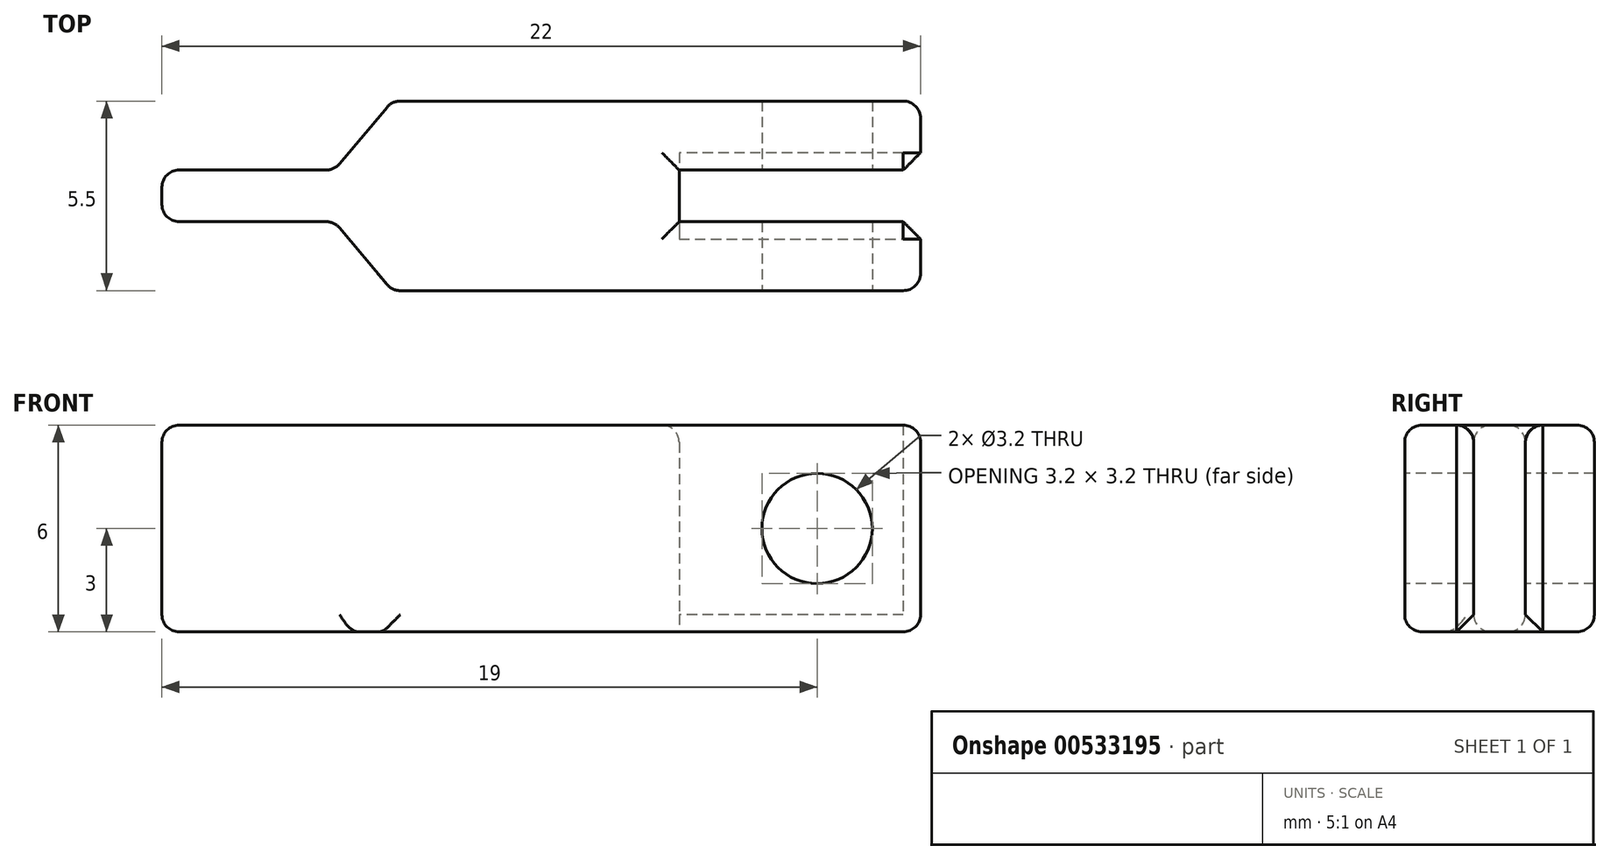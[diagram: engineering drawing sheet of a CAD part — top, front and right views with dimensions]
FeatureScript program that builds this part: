
annotation { "Feature Type Name" : "Feature", "Feature Type Description" : "" }
export const myFeature = defineFeature(function(context is Context, id is Id, definition is map)
    precondition{}
    {
        {
            var Q0;
            Q0=qCreatedBy(makeId("Top.planeOp"),FACE);
            var sketch = newSketch(context, id + "F0", { "sketchPlane" : qUnion([Q0])});
            skLineSegment(sketch, "E0", {"start": v(0, 0) * mm, "end": v(-15.32, 0) * mm});
            skLineSegment(sketch, "E1", {"start": v(-15.32, 0) * mm, "end": v(-17, 2) * mm});
            skLineSegment(sketch, "E2", {"start": v(-17, 2) * mm, "end": v(-22, 2) * mm});
            skLineSegment(sketch, "E3", {"start": v(-22, 2) * mm, "end": v(-22, 3.5) * mm});
            skLineSegment(sketch, "E4", {"start": v(-22, 3.5) * mm, "end": v(-17, 3.5) * mm});
            skLineSegment(sketch, "E5", {"start": v(-17, 3.5) * mm, "end": v(-15.32, 5.5) * mm});
            skLineSegment(sketch, "E6", {"start": v(-15.32, 5.5) * mm, "end": v(0, 5.5) * mm});
            skLineSegment(sketch, "E7", {"start": v(0, 5.5) * mm, "end": v(0, 3.5) * mm});
            skLineSegment(sketch, "E8", {"start": v(0, 3.5) * mm, "end": v(-7, 3.5) * mm});
            skLineSegment(sketch, "E9", {"start": v(-7, 3.5) * mm, "end": v(-7, 2) * mm});
            skLineSegment(sketch, "E10", {"start": v(-7, 2) * mm, "end": v(0, 2) * mm});
            skLineSegment(sketch, "E11", {"start": v(0, 2) * mm, "end": v(0, 0) * mm});
            skSolve(sketch);
        }
        {
            var Q0;
            Q0=makeQuery(id+"F0.imprint","IMPRINT",FACE,{"disambiguationData":[TD([[makeQuery(id+"F0.imprint","IMPRINT",EDGE,{"derivedFrom":sQuery(id+"F0.wireOp",EDGE,"E0")}),-1.0]])]});
            extrude(context, id + "F1", {"entities" : qUnion([Q0]), "depth" : 6 * mm, "offsetDistance" : 25 * mm});
        }
        {
            var Q0;
            Q0=makeQuery(id+"F1.opExtrude","SWEPT_FACE",FACE,{"disambiguationData":[OSD([sQuery(id+"F0.wireOp",EDGE,"E0")])]});
            var sketch = newSketch(context, id + "F2", { "sketchPlane" : qUnion([Q0])});
            skLineSegment(sketch, "E12", {"start": v(0, 3) * mm, "end": v(-15.32, 3) * mm, "construction": true});
            skCircle(sketch, "E13", {"center": v(-3, 3) * mm, "radius": 1.6 * mm});
            skSolve(sketch);
        }
        {
            var Q0;
            Q0=sQuery(id+"F2.wireOp",VERTEX,"E13.center");
            var Q1;
            Q1=makeQuery(id+"F1.opExtrude","SWEPT_BODY",BODY,{"disambiguationData":[OSD([sQuery(id+"F0.wireOp",EDGE,"E0"),sQuery(id+"F0.wireOp",EDGE,"E1"),sQuery(id+"F0.wireOp",EDGE,"E2"),sQuery(id+"F0.wireOp",EDGE,"E3"),sQuery(id+"F0.wireOp",EDGE,"E4"),sQuery(id+"F0.wireOp",EDGE,"E5"),sQuery(id+"F0.wireOp",EDGE,"E6"),sQuery(id+"F0.wireOp",EDGE,"E7"),sQuery(id+"F0.wireOp",EDGE,"E8"),sQuery(id+"F0.wireOp",EDGE,"E9"),sQuery(id+"F0.wireOp",EDGE,"E10"),sQuery(id+"F0.wireOp",EDGE,"E11")])]});
            hole(context, id + "F3", {"style" : HoleStyle.SIMPLE, "endStyle" : HoleEndStyle.THROUGH, "holeDiameter" : 3.2 * mm, "isTappedThrough" : true, "tappedDepth" : 12 * mm, "tapClearance" : 3, "locations" : qUnion([Q0]), "scope" : qUnion([Q1])});
        }
        {
            var Q0;
            Q0=makeQuery(id+"F1.opExtrude","SWEPT_EDGE",EDGE,{"disambiguationData":[OSD([sQuery(id+"F0.wireOp",EDGE,"E1"),sQuery(id+"F0.wireOp",EDGE,"E2")])]});
            var Q1;
            Q1=makeQuery(id+"F1.opExtrude","SWEPT_EDGE",EDGE,{"disambiguationData":[OSD([sQuery(id+"F0.wireOp",EDGE,"E0"),sQuery(id+"F0.wireOp",EDGE,"E1")])]});
            var Q2;
            Q2=makeQuery(id+"F1.opExtrude","SWEPT_EDGE",EDGE,{"disambiguationData":[OSD([sQuery(id+"F0.wireOp",EDGE,"E0"),sQuery(id+"F0.wireOp",EDGE,"E11")])]});
            var Q3;
            Q3=makeQuery(id+"F1.opExtrude","SWEPT_EDGE",EDGE,{"disambiguationData":[OSD([sQuery(id+"F0.wireOp",EDGE,"E6"),sQuery(id+"F0.wireOp",EDGE,"E7")])]});
            var Q4;
            Q4=makeQuery(id+"F1.opExtrude","SWEPT_EDGE",EDGE,{"disambiguationData":[OSD([sQuery(id+"F0.wireOp",EDGE,"E5"),sQuery(id+"F0.wireOp",EDGE,"E6")])]});
            var Q5;
            Q5=makeQuery(id+"F1.opExtrude","SWEPT_EDGE",EDGE,{"disambiguationData":[OSD([sQuery(id+"F0.wireOp",EDGE,"E4"),sQuery(id+"F0.wireOp",EDGE,"E5")])]});
            var Q6;
            Q6=makeQuery(id+"F1.opExtrude","CAP_EDGE",EDGE,{"disambiguationData":[OSD([sQuery(id+"F0.wireOp",EDGE,"E6")])],"isStart":true});
            var Q7;
            Q7=makeQuery(id+"F1.opExtrude","CAP_EDGE",EDGE,{"disambiguationData":[OSD([sQuery(id+"F0.wireOp",EDGE,"E5")])],"isStart":true});
            var Q8;
            Q8=makeQuery(id+"F1.opExtrude","CAP_EDGE",EDGE,{"disambiguationData":[OSD([sQuery(id+"F0.wireOp",EDGE,"E4")])],"isStart":true});
            var Q9;
            Q9=makeQuery(id+"F1.opExtrude","CAP_EDGE",EDGE,{"disambiguationData":[OSD([sQuery(id+"F0.wireOp",EDGE,"E2")])],"isStart":true});
            var Q10;
            Q10=makeQuery(id+"F1.opExtrude","CAP_EDGE",EDGE,{"disambiguationData":[OSD([sQuery(id+"F0.wireOp",EDGE,"E0")])],"isStart":true});
            var Q11;
            Q11=makeQuery(id+"F1.opExtrude","CAP_EDGE",EDGE,{"disambiguationData":[OSD([sQuery(id+"F0.wireOp",EDGE,"E11")])],"isStart":true});
            var Q12;
            Q12=makeQuery(id+"F1.opExtrude","CAP_EDGE",EDGE,{"disambiguationData":[OSD([sQuery(id+"F0.wireOp",EDGE,"E7")])],"isStart":true});
            var Q13;
            Q13=makeQuery(id+"F1.opExtrude","CAP_FACE",FACE,{"disambiguationData":[OSD([sQuery(id+"F0.wireOp",EDGE,"E0"),sQuery(id+"F0.wireOp",EDGE,"E1"),sQuery(id+"F0.wireOp",EDGE,"E2"),sQuery(id+"F0.wireOp",EDGE,"E3"),sQuery(id+"F0.wireOp",EDGE,"E4"),sQuery(id+"F0.wireOp",EDGE,"E5"),sQuery(id+"F0.wireOp",EDGE,"E6"),sQuery(id+"F0.wireOp",EDGE,"E7"),sQuery(id+"F0.wireOp",EDGE,"E8"),sQuery(id+"F0.wireOp",EDGE,"E9"),sQuery(id+"F0.wireOp",EDGE,"E10"),sQuery(id+"F0.wireOp",EDGE,"E11")])],"isStart":false});
            var Q14;
            Q14=makeQuery(id+"F1.opExtrude","CAP_EDGE",EDGE,{"disambiguationData":[OSD([sQuery(id+"F0.wireOp",EDGE,"E3")])],"isStart":false});
            var Q15;
            Q15=makeQuery(id+"F1.opExtrude","CAP_EDGE",EDGE,{"disambiguationData":[OSD([sQuery(id+"F0.wireOp",EDGE,"E3")])],"isStart":true});
            var Q16;
            Q16=makeQuery(id+"F1.opExtrude","SWEPT_EDGE",EDGE,{"disambiguationData":[OSD([sQuery(id+"F0.wireOp",EDGE,"E2"),sQuery(id+"F0.wireOp",EDGE,"E3")])]});
            var Q17;
            Q17=makeQuery(id+"F1.opExtrude","SWEPT_EDGE",EDGE,{"disambiguationData":[OSD([sQuery(id+"F0.wireOp",EDGE,"E3"),sQuery(id+"F0.wireOp",EDGE,"E4")])]});
            fillet(context, id + "F4", {"entities" : qUnion([Q0, Q1, Q2, Q3, Q4, Q5, Q6, Q7, Q8, Q9, Q10, Q11, Q12, Q13, Q14, Q15, Q16, Q17]), "radius" : 0.5 * mm, "tangentPropagation" : true, "allowEdgeOverflow" : false});
        }
        {
            var Q0;
            Q0=makeQuery(id+"F1.opExtrude","SWEPT_EDGE",EDGE,{"disambiguationData":[OSD([sQuery(id+"F0.wireOp",EDGE,"E10"),sQuery(id+"F0.wireOp",EDGE,"E11")])]});
            var Q1;
            Q1=makeQuery(id+"F1.opExtrude","SWEPT_EDGE",EDGE,{"disambiguationData":[OSD([sQuery(id+"F0.wireOp",EDGE,"E7"),sQuery(id+"F0.wireOp",EDGE,"E8")])]});
            chamfer(context, id + "F5", {"entities" : qUnion([Q0, Q1]), "width" : 0.5 * mm, "tangentPropagation" : true});
        }
    });
